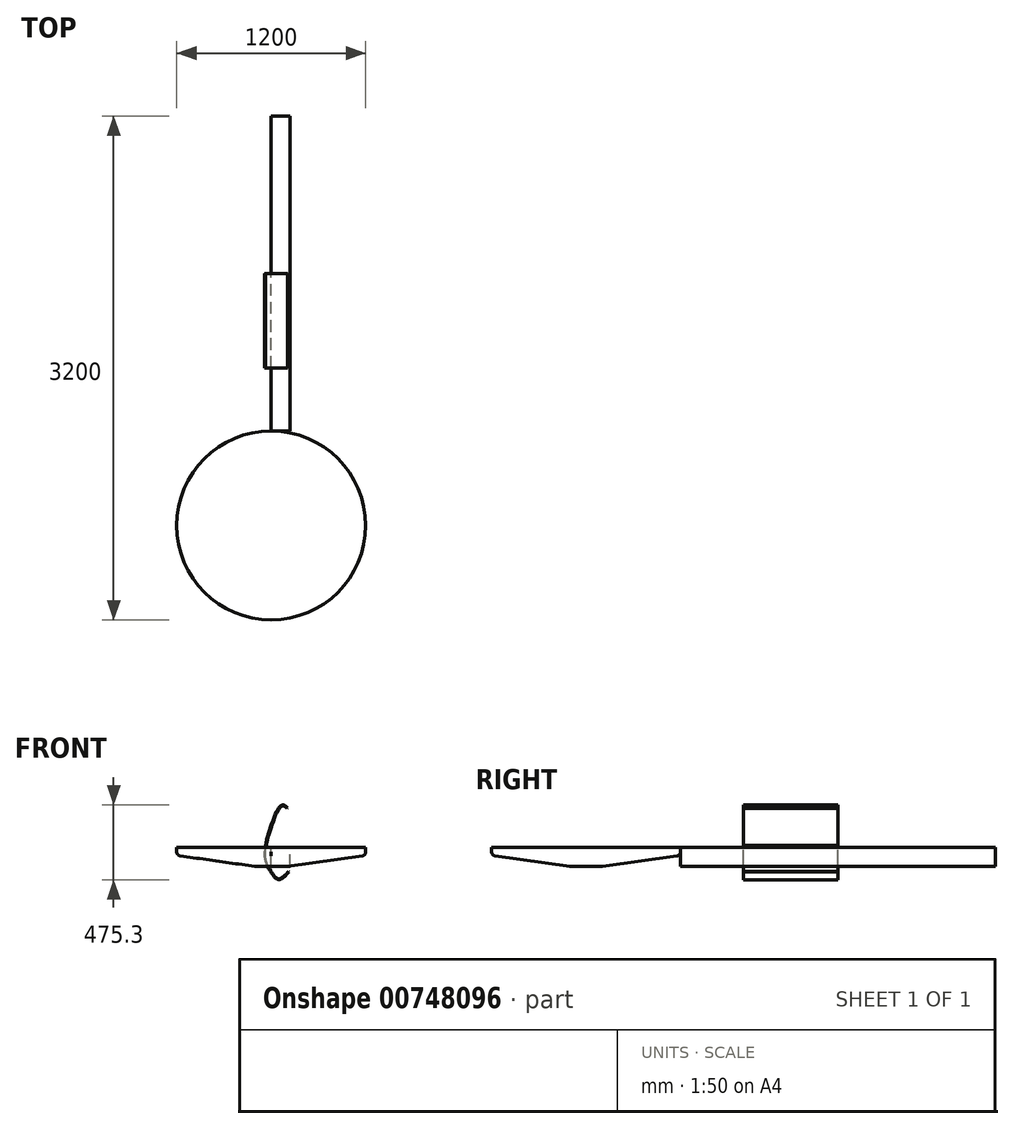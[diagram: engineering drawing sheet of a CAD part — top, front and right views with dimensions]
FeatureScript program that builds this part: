
annotation { "Feature Type Name" : "Feature", "Feature Type Description" : "" }
export const myFeature = defineFeature(function(context is Context, id is Id, definition is map)
    precondition{}
    {
        {
            var Q0;
            Q0=qCreatedBy(makeId("Front.planeOp"),FACE);
            var sketch = newSketch(context, id + "F0", { "sketchPlane" : qUnion([Q0])});
            skLineSegment(sketch, "E0.bottom", {"start": v(0, 0) * mm, "end": v(120, 0) * mm});
            skLineSegment(sketch, "E0.top", {"start": v(0, 120) * mm, "end": v(120, 120) * mm});
            skLineSegment(sketch, "E0.left", {"start": v(0, 0) * mm, "end": v(0, 120) * mm});
            skLineSegment(sketch, "E0.right", {"start": v(120, 0) * mm, "end": v(120, 120) * mm});
            skSolve(sketch);
        }
        {
            var Q0;
            Q0 = qSketchRegion(id + "F0", true);
            extrude(context, id + "F1", {"entities" : qUnion([Q0]), "endBound" : BoundingType.SYMMETRIC, "depth" : 2000 * mm, "offsetDistance" : 25 * mm});
        }
        {
            var Q0;
            Q0=qCreatedBy(makeId("Front.planeOp"),FACE);
            var sketch = newSketch(context, id + "F2", { "sketchPlane" : qUnion([Q0])});
            skFitSpline(sketch, "E1", {"points": [v(112.5, -34.68) * mm, v(46.95, -84.66) * mm, v(0, -39.87) * mm, v(-33.54, 25.04) * mm, v(-36.14, 134.1) * mm, v(50.84, 374.91) * mm, v(79.4, 389.84) * mm, v(104.72, 371.02) * mm], "startDerivative": vector(-476.69, -538.67) * mm, "endDerivative": vector(281.95, -277.4) * mm});
            skFitSpline(sketch, "E2.0", {"points": [v(108.76, -31.37) * mm, v(103.8, -36.98) * mm, v(96.38, -45.35) * mm, v(86.67, -55.58) * mm, v(79.52, -62.57) * mm, v(72.53, -68.64) * mm, v(65.79, -73.6) * mm, v(60.45, -76.6) * mm, v(56.4, -78.28) * mm, v(53.5, -79.15) * mm, v(50.75, -79.65) * mm, v(48.55, -79.75) * mm, v(46.86, -79.65) * mm, v(45.16, -79.42) * mm, v(43.01, -78.9) * mm, v(40.39, -77.9) * mm, v(36.82, -76.07) * mm, v(32.26, -72.85) * mm, v(26.74, -67.7) * mm, v(21.28, -61.52) * mm, v(15.92, -54.56) * mm, v(11.56, -48.34) * mm, v(8.16, -43.25) * mm, v(5.64, -39.4) * mm, v(3.17, -35.56) * mm, v(0.74, -31.76) * mm, v(-1.62, -28) * mm, v(-4.7, -23.03) * mm, v(-8.39, -16.88) * mm, v(-12.56, -9.58) * mm, v(-17.76, 0.1) * mm, v(-22.4, 9.81) * mm, v(-26.4, 19.69) * mm, v(-29.07, 27.22) * mm, v(-31.4, 34.93) * mm, v(-34, 45.53) * mm, v(-36.3, 59.65) * mm, v(-37.09, 75.55) * mm, v(-36.7, 89.69) * mm, v(-35.87, 101.09) * mm, v(-34.7, 111.32) * mm, v(-33.46, 120) * mm, v(-32.38, 126.75) * mm, v(-31.13, 133.77) * mm, v(-29.73, 141.06) * mm, v(-28.16, 148.6) * mm, v(-25.88, 158.94) * mm, v(-22.68, 172.37) * mm, v(-18.33, 189.08) * mm, v(-13.54, 206.2) * mm, v(-6.63, 229.34) * mm, v(2.83, 258.35) * mm, v(15.02, 291.78) * mm, v(25.49, 317.24) * mm, v(33.8, 335.4) * mm, v(39.93, 347.72) * mm, v(44.9, 356.74) * mm, v(48.75, 363.1) * mm, v(51.57, 367.4) * mm, v(54.29, 371.24) * mm, v(56.9, 374.55) * mm, v(59.4, 377.37) * mm, v(62.58, 380.5) * mm, v(65.51, 382.72) * mm, v(68.18, 384.17) * mm, v(70.05, 384.93) * mm, v(71.81, 385.39) * mm, v(73.5, 385.6) * mm, v(75.18, 385.58) * mm, v(76.88, 385.35) * mm, v(78.63, 384.89) * mm, v(81.06, 383.97) * mm, v(84.28, 382.24) * mm, v(88.35, 379.34) * mm, v(92.54, 375.78) * mm, v(96.83, 371.76) * mm, v(99.74, 368.9) * mm, v(101.21, 367.45) * mm]});
            skLineSegment(sketch, "E3", {"start": v(101.21, 367.45) * mm, "end": v(104.72, 371.02) * mm});
            skLineSegment(sketch, "E4", {"start": v(-36.14, 134.1) * mm, "end": v(-31.05, 134.1) * mm});
            skLineSegment(sketch, "E5", {"start": v(108.76, -31.37) * mm, "end": v(112.5, -34.68) * mm});
            skSolve(sketch);
        }
        {
            var Q0;
            {var subQ0=sQuery(id+"F2.wireOp",EDGE,"E3");Q0=makeQuery(id+"F2.imprint","IMPRINT",FACE,{"disambiguationData":[TD([[makeQuery(id+"F2.imprint","IMPRINT",EDGE,{"derivedFrom":subQ0}),1.0]])]});}
            extrude(context, id + "F3", {"entities" : qUnion([Q0]), "depth" : 600 * mm, "offsetDistance" : 25 * mm});
        }
        {
            var Q0;
            {var subQ2=sQuery(id+"F2.wireOp",EDGE,"E4");Q0=makeQuery(id+"F2.imprint","IMPRINT",FACE,{"disambiguationData":[TD([[makeQuery(id+"F2.imprint","IMPRINT",EDGE,{"derivedFrom":subQ2}),-1.0]])]});}
            extrude(context, id + "F4", {"entities" : qUnion([Q0]), "depth" : 600 * mm, "offsetDistance" : 25 * mm});
        }
        {
            var Q0;
            Q0=makeQuery(id+"F1.opExtrude","SWEPT_FACE",FACE,{"disambiguationData":[OSD([sQuery(id+"F0.wireOp",EDGE,"E0.left")])]});
            var sketch = newSketch(context, id + "F5", { "sketchPlane" : qUnion([Q0])});
            skLineSegment(sketch, "E6", {"start": v(1000, 120) * mm, "end": v(1000, 91.73) * mm});
            skLineSegment(sketch, "E7", {"start": v(1021.52, 66.98) * mm, "end": v(1496.52, 0.24) * mm});
            skLineSegment(sketch, "E8", {"start": v(1500, 0) * mm, "end": v(1600, 0) * mm});
            skPoint(sketch, "E9.visualSharp", {"position": v(1000, 70) * mm});
            skArc(sketch, "E9.filletArc", {"start": v(1000, 91.73) * mm, "mid": v(1006.13, 75.33) * mm, "end": v(1021.52, 66.98) * mm});
            skPoint(sketch, "E10.visualSharp", {"position": v(1498.25, 0) * mm});
            skArc(sketch, "E10.filletArc", {"start": v(1496.52, 0.24) * mm, "mid": v(1498.97, 0.02) * mm, "end": v(1501.43, 0.04) * mm});
            skArc(sketch, "E11.filletArc", {"start": v(1496.52, 0.24) * mm, "mid": v(1498.26, 0.06) * mm, "end": v(1500, 0) * mm});
            skLineSegment(sketch, "E12", {"start": v(1600, 0) * mm, "end": v(1600, 232.98) * mm, "construction": true});
            skLineSegment(sketch, "E13", {"start": v(1000, 120) * mm, "end": v(1600, 120) * mm});
            skLineSegment(sketch, "E14", {"start": v(1600, 120) * mm, "end": v(1600, 0) * mm});
            skSolve(sketch);
        }
        {
            var Q0;
            Q0 = qSketchRegion(id + "F5", true);
            var Q1;
            Q1=sQuery(id+"F5.wireOp",EDGE,"E12");
            revolve(context, id + "F6", {"surfaceOperationType" : NewSurfaceOperationType.NEW, "entities" : qUnion([Q0]), "axis" : qUnion([Q1]), "revolveType" : RevolveType.FULL});
        }
    });
